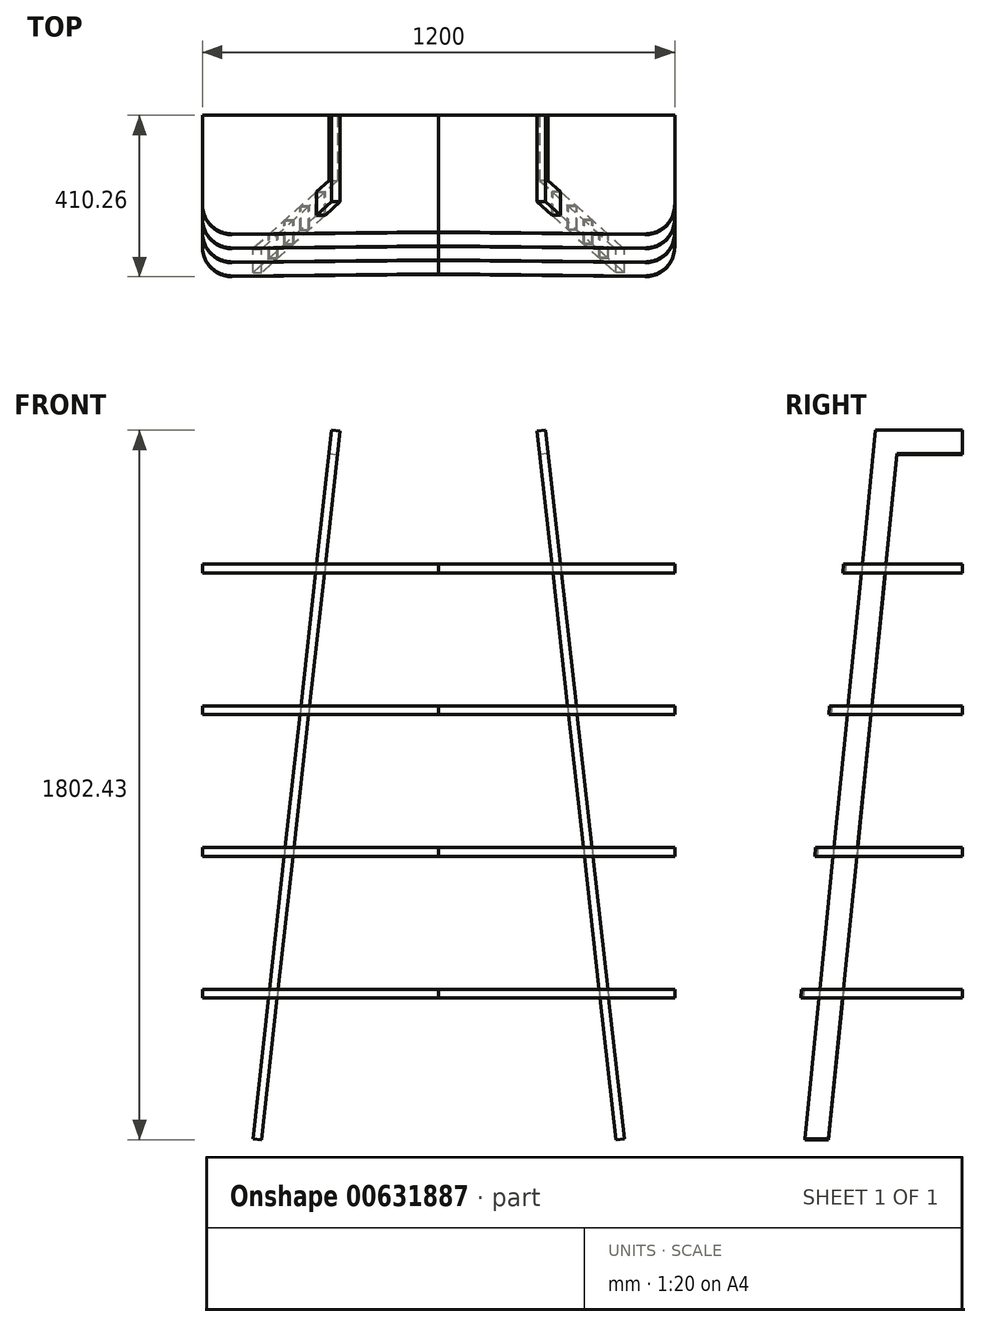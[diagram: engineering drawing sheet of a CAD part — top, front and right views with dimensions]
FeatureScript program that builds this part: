
annotation { "Feature Type Name" : "Feature", "Feature Type Description" : "" }
export const myFeature = defineFeature(function(context is Context, id is Id, definition is map)
    precondition{}
    {
        {
            var Q0;
            Q0=qCreatedBy(makeId("Front.planeOp"),FACE);
            var sketch = newSketch(context, id + "F0", { "sketchPlane" : qUnion([Q0])});
            skLineSegment(sketch, "E0.bottom", {"start": v(0, 0) * mm, "end": v(600, 0) * mm, "construction": true});
            skLineSegment(sketch, "E0.top", {"start": v(0, 1800) * mm, "end": v(600, 1800) * mm, "construction": true});
            skLineSegment(sketch, "E0.left", {"start": v(0, 0) * mm, "end": v(0, 1800) * mm, "construction": true});
            skLineSegment(sketch, "E0.right", {"start": v(600, 0) * mm, "end": v(600, 1800) * mm, "construction": true});
            skLineSegment(sketch, "E1", {"start": v(450, 0) * mm, "end": v(250, 1800) * mm, "construction": true});
            skLineSegment(sketch, "E2", {"start": v(0, 360) * mm, "end": v(600, 360) * mm, "construction": true});
            skLineSegment(sketch, "E3.0.1.0", {"start": v(0, 720) * mm, "end": v(600, 720) * mm, "construction": true});
            skLineSegment(sketch, "E3.0.2.0", {"start": v(0, 1080) * mm, "end": v(600, 1080) * mm, "construction": true});
            skLineSegment(sketch, "E3.0.3.0", {"start": v(0, 1440) * mm, "end": v(600, 1440) * mm, "construction": true});
            skLineSegment(sketch, "E3.direction1", {"start": v(0, 360) * mm, "end": v(0, 360) * mm});
            skLineSegment(sketch, "E3.direction2", {"start": v(0, 360) * mm, "end": v(0, 720) * mm, "construction": true});
            skLineSegment(sketch, "E4.bottom", {"start": v(0, 360) * mm, "end": v(600, 360) * mm});
            skLineSegment(sketch, "E4.top", {"start": v(0, 382) * mm, "end": v(600, 382) * mm});
            skLineSegment(sketch, "E4.left", {"start": v(0, 360) * mm, "end": v(0, 382) * mm});
            skLineSegment(sketch, "E4.right", {"start": v(600, 360) * mm, "end": v(600, 382) * mm});
            skLineSegment(sketch, "E5.0.1.0", {"start": v(0, 742) * mm, "end": v(600, 742) * mm});
            skLineSegment(sketch, "E5.0.1.2", {"start": v(0, 720) * mm, "end": v(600, 720) * mm});
            skLineSegment(sketch, "E5.0.1.3", {"start": v(600, 720) * mm, "end": v(600, 742) * mm});
            skLineSegment(sketch, "E5.0.1.4", {"start": v(0, 720) * mm, "end": v(0, 742) * mm});
            skLineSegment(sketch, "E5.0.2.0", {"start": v(0, 1102) * mm, "end": v(600, 1102) * mm});
            skLineSegment(sketch, "E5.0.2.2", {"start": v(0, 1080) * mm, "end": v(600, 1080) * mm});
            skLineSegment(sketch, "E5.0.2.3", {"start": v(600, 1080) * mm, "end": v(600, 1102) * mm});
            skLineSegment(sketch, "E5.0.2.4", {"start": v(0, 1080) * mm, "end": v(0, 1102) * mm});
            skLineSegment(sketch, "E5.0.3.0", {"start": v(0, 1462) * mm, "end": v(600, 1462) * mm});
            skLineSegment(sketch, "E5.0.3.2", {"start": v(0, 1440) * mm, "end": v(600, 1440) * mm});
            skLineSegment(sketch, "E5.0.3.3", {"start": v(600, 1440) * mm, "end": v(600, 1462) * mm});
            skLineSegment(sketch, "E5.0.3.4", {"start": v(0, 1440) * mm, "end": v(0, 1462) * mm});
            skLineSegment(sketch, "E5.direction1", {"start": v(0, 360) * mm, "end": v(25, 360) * mm, "construction": true});
            skSolve(sketch);
        }
        {
            var Q0;
            Q0=sQuery(id+"F0.wireOp",EDGE,"E1");
            cPlane(context, id + "F1", {"entities" : qUnion([Q0]), "cplaneType" : CPlaneType.LINE_ANGLE, "offset" : 25 * mm, "angle" : 0 * degree, "width" : 150 * mm, "height" : 150 * mm});
        }
        {
            var Q0;
            Q0=qCreatedBy(id+"F1.planeOp",FACE);
            var sketch = newSketch(context, id + "F2", { "sketchPlane" : qUnion([Q0])});
            skLineSegment(sketch, "E6.0", {"start": v(0, -49.7) * mm, "end": v(0, 1761.38) * mm, "construction": true});
            skLineSegment(sketch, "E7.bottom", {"start": v(0, 1761.38) * mm, "end": v(-400, 1761.38) * mm, "construction": true});
            skLineSegment(sketch, "E7.top", {"start": v(0, -49.7) * mm, "end": v(-400, -49.7) * mm, "construction": true});
            skLineSegment(sketch, "E7.left", {"start": v(0, 1761.38) * mm, "end": v(0, -49.7) * mm, "construction": true});
            skLineSegment(sketch, "E7.right", {"start": v(-400, 1761.38) * mm, "end": v(-400, -49.7) * mm, "construction": true});
            skLineSegment(sketch, "E8", {"start": v(0, 1761.38) * mm, "end": v(-220, 1761.38) * mm});
            skLineSegment(sketch, "E9", {"start": v(-220, 1761.38) * mm, "end": v(-400, -49.7) * mm});
            skLineSegment(sketch, "E10.0", {"start": v(-165.67, 1701.38) * mm, "end": v(-339.7, -49.7) * mm});
            skLineSegment(sketch, "E10.1", {"start": v(0, 1701.38) * mm, "end": v(-165.67, 1701.38) * mm});
            skLineSegment(sketch, "E11", {"start": v(-400, -49.7) * mm, "end": v(-339.7, -49.7) * mm});
            skLineSegment(sketch, "E12", {"start": v(0, 1761.38) * mm, "end": v(0, 1701.38) * mm});
            skSolve(sketch);
        }
        {
            var Q0;
            Q0 = qSketchRegion(id + "F2", true);
            extrude(context, id + "F3", {"entities" : qUnion([Q0]), "depth" : 22 * mm, "offsetDistance" : 25 * mm});
        }
        {
            var Q0;
            Q0=makeQuery(id+"F0.imprint","IMPRINT",FACE,{"disambiguationData":[TD([[makeQuery(id+"F0.imprint","IMPRINT",EDGE,{"derivedFrom":sQuery(id+"F0.wireOp",EDGE,"E4.bottom")}),1.0]])]});
            var Q1;
            Q1=makeQuery(id+"F0.imprint","IMPRINT",FACE,{"disambiguationData":[TD([[makeQuery(id+"F0.imprint","IMPRINT",EDGE,{"derivedFrom":sQuery(id+"F0.wireOp",EDGE,"E5.0.1.0")}),-1.0]])]});
            var Q2;
            Q2=makeQuery(id+"F0.imprint","IMPRINT",FACE,{"disambiguationData":[TD([[makeQuery(id+"F0.imprint","IMPRINT",EDGE,{"derivedFrom":sQuery(id+"F0.wireOp",EDGE,"E5.0.2.0")}),-1.0]])]});
            var Q3;
            Q3=makeQuery(id+"F0.imprint","IMPRINT",FACE,{"disambiguationData":[TD([[makeQuery(id+"F0.imprint","IMPRINT",EDGE,{"derivedFrom":sQuery(id+"F0.wireOp",EDGE,"E5.0.3.0")}),-1.0]])]});
            var Q4;
            Q4=makeQuery(id+"F3.opExtrude","SWEPT_FACE",FACE,{"disambiguationData":[OSD([sQuery(id+"F2.wireOp",EDGE,"E9")])]});
            extrude(context, id + "F4", {"entities" : qUnion([Q0, Q1, Q2, Q3]), "endBound" : BoundingType.UP_TO_SURFACE, "depth" : 25 * mm, "endBoundEntityFace" : qUnion([Q4]), "hasOffset" : true, "offsetDistance" : 45 * mm, "offsetOppositeDirection" : true});
        }
        {
            var Q0;
            Q0=makeQuery(id+"F3.opExtrude","SWEPT_BODY",BODY,{"disambiguationData":[OSD([sQuery(id+"F2.wireOp",EDGE,"E8"),sQuery(id+"F2.wireOp",EDGE,"E9"),sQuery(id+"F2.wireOp",EDGE,"E10.0"),sQuery(id+"F2.wireOp",EDGE,"E10.1"),sQuery(id+"F2.wireOp",EDGE,"E11"),sQuery(id+"F2.wireOp",EDGE,"E12")])]});
            var Q1;
            Q1=makeQuery(id+"F4.opExtrude","SWEPT_BODY",BODY,{"disambiguationData":[OSD([sQuery(id+"F0.wireOp",EDGE,"E5.0.3.0"),sQuery(id+"F0.wireOp",EDGE,"E5.0.3.2"),sQuery(id+"F0.wireOp",EDGE,"E5.0.3.3"),sQuery(id+"F0.wireOp",EDGE,"E5.0.3.4")])]});
            var Q2;
            Q2=makeQuery(id+"F4.opExtrude","SWEPT_BODY",BODY,{"disambiguationData":[OSD([sQuery(id+"F0.wireOp",EDGE,"E5.0.2.0"),sQuery(id+"F0.wireOp",EDGE,"E5.0.2.2"),sQuery(id+"F0.wireOp",EDGE,"E5.0.2.3"),sQuery(id+"F0.wireOp",EDGE,"E5.0.2.4")])]});
            var Q3;
            Q3=makeQuery(id+"F4.opExtrude","SWEPT_BODY",BODY,{"disambiguationData":[OSD([sQuery(id+"F0.wireOp",EDGE,"E5.0.1.0"),sQuery(id+"F0.wireOp",EDGE,"E5.0.1.2"),sQuery(id+"F0.wireOp",EDGE,"E5.0.1.3"),sQuery(id+"F0.wireOp",EDGE,"E5.0.1.4")])]});
            var Q4;
            Q4=makeQuery(id+"F4.opExtrude","SWEPT_BODY",BODY,{"disambiguationData":[OSD([sQuery(id+"F0.wireOp",EDGE,"E4.bottom"),sQuery(id+"F0.wireOp",EDGE,"E4.top"),sQuery(id+"F0.wireOp",EDGE,"E4.left"),sQuery(id+"F0.wireOp",EDGE,"E4.right")])]});
            booleanBodies(context, id + "F5", {"operationType" : BooleanOperationType.SUBTRACTION, "tools" : qUnion([Q0]), "targets" : qUnion([Q1, Q2, Q3, Q4]), "keepTools" : true});
        }
        {
            var Q0;
            Q0=makeQuery(id+"F4.opExtrude","CAP_EDGE",EDGE,{"disambiguationData":[OSD([sQuery(id+"F0.wireOp",EDGE,"E4.right")])],"isStart":false});
            var Q1;
            Q1=makeQuery(id+"F4.opExtrude","CAP_EDGE",EDGE,{"disambiguationData":[OSD([sQuery(id+"F0.wireOp",EDGE,"E5.0.1.3")])],"isStart":false});
            var Q2;
            Q2=makeQuery(id+"F4.opExtrude","CAP_EDGE",EDGE,{"disambiguationData":[OSD([sQuery(id+"F0.wireOp",EDGE,"E5.0.2.3")])],"isStart":false});
            var Q3;
            Q3=makeQuery(id+"F4.opExtrude","CAP_EDGE",EDGE,{"disambiguationData":[OSD([sQuery(id+"F0.wireOp",EDGE,"E5.0.3.3")])],"isStart":false});
            fillet(context, id + "F6", {"entities" : qUnion([Q0, Q1, Q2, Q3]), "radius" : 75 * mm, "tangentPropagation" : true, "allowEdgeOverflow" : false});
        }
        {
            var Q0;
            Q0=makeQuery(id+"F3.opExtrude","SWEPT_BODY",BODY,{"disambiguationData":[OSD([sQuery(id+"F2.wireOp",EDGE,"E8"),sQuery(id+"F2.wireOp",EDGE,"E9"),sQuery(id+"F2.wireOp",EDGE,"E10.0"),sQuery(id+"F2.wireOp",EDGE,"E10.1"),sQuery(id+"F2.wireOp",EDGE,"E11"),sQuery(id+"F2.wireOp",EDGE,"E12")])]});
            var Q1;
            Q1=makeQuery(id+"F4.opExtrude","SWEPT_BODY",BODY,{"disambiguationData":[OSD([sQuery(id+"F0.wireOp",EDGE,"E4.bottom"),sQuery(id+"F0.wireOp",EDGE,"E4.top"),sQuery(id+"F0.wireOp",EDGE,"E4.left"),sQuery(id+"F0.wireOp",EDGE,"E4.right")])]});
            var Q2;
            Q2=makeQuery(id+"F4.opExtrude","SWEPT_BODY",BODY,{"disambiguationData":[OSD([sQuery(id+"F0.wireOp",EDGE,"E5.0.1.0"),sQuery(id+"F0.wireOp",EDGE,"E5.0.1.2"),sQuery(id+"F0.wireOp",EDGE,"E5.0.1.3"),sQuery(id+"F0.wireOp",EDGE,"E5.0.1.4")])]});
            var Q3;
            Q3=makeQuery(id+"F4.opExtrude","SWEPT_BODY",BODY,{"disambiguationData":[OSD([sQuery(id+"F0.wireOp",EDGE,"E5.0.2.0"),sQuery(id+"F0.wireOp",EDGE,"E5.0.2.2"),sQuery(id+"F0.wireOp",EDGE,"E5.0.2.3"),sQuery(id+"F0.wireOp",EDGE,"E5.0.2.4")])]});
            var Q4;
            Q4=makeQuery(id+"F4.opExtrude","SWEPT_BODY",BODY,{"disambiguationData":[OSD([sQuery(id+"F0.wireOp",EDGE,"E5.0.3.0"),sQuery(id+"F0.wireOp",EDGE,"E5.0.3.2"),sQuery(id+"F0.wireOp",EDGE,"E5.0.3.3"),sQuery(id+"F0.wireOp",EDGE,"E5.0.3.4")])]});
            var Q5;
            Q5=makeQuery(id+"F4.opExtrude","SWEPT_FACE",FACE,{"disambiguationData":[OSD([sQuery(id+"F0.wireOp",EDGE,"E5.0.2.4")])]});
            mirror(context, id + "F7", {"entities" : qUnion([Q0, Q1, Q2, Q3, Q4]), "mirrorPlane" : qUnion([Q5])});
        }
    });
